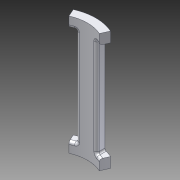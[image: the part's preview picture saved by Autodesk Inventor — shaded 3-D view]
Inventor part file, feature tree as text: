
AUTODESK INVENTOR PART (.ipt)
format: ipt  version: 2012 (Build 160160000, 160)  size: 157,184 bytes
history: native  units: mm
features: extrude x3, mirror x2, fillet x2, sketch x1
ambient origin geometry x8: Origin, YZ Plane, XZ Plane, XY Plane, X Axis, Y Axis, Z Axis, Center Point
bodies: Solid1 (feature_tree)
feature tree (8):
  sketch  "Sketch1"  dims[d0=48.0mm d1=40.0mm d2=6.0mm d7=22.0mm d8=27.0mm d9=70.0mm d10=0.0mm d11=58.0mm d12=0.0mm d13=2.0mm d14=25.0mm d23=68.0mm d24=0.0mm d25=4.18879mm d26=1.0mm d27=1.5mm]
  extrude  "Extrusion1"  Depth=40.0mm
  extrude  "Extrusion2"  Depth=6.0mm
  mirror  "Mirror1"
  extrude  "Extrusion3"  Depth=22.0mm
  mirror  "Mirror2"
  fillet  "Fillet1"  Radius=27.0mm
  fillet  "Fillet2"  Radius=70.0mm
